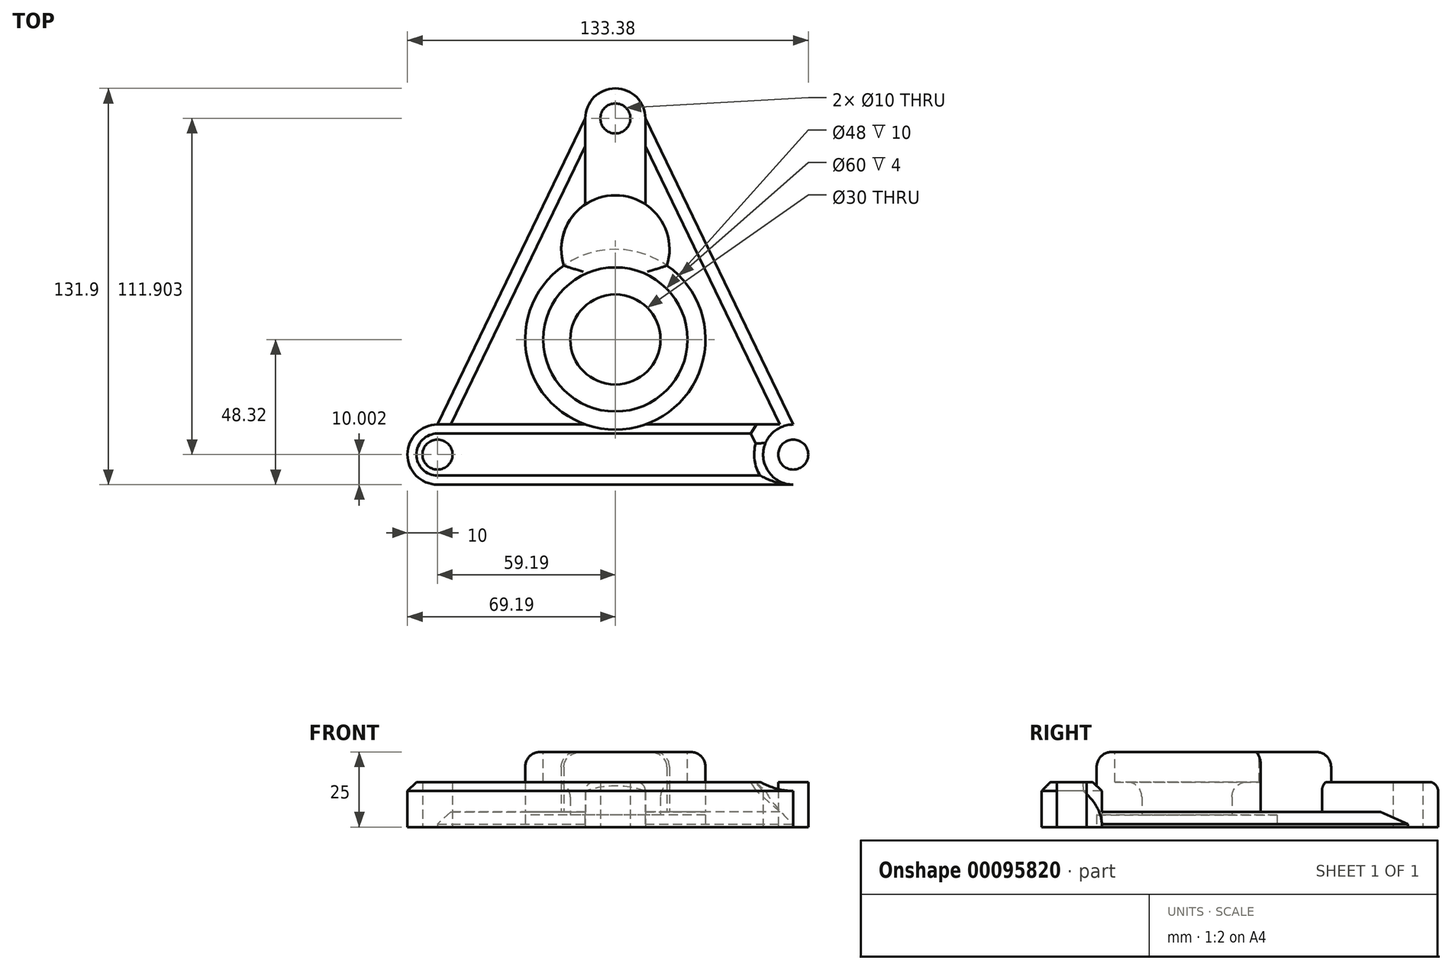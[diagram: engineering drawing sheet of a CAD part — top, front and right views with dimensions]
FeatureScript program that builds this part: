
annotation { "Feature Type Name" : "Feature", "Feature Type Description" : "" }
export const myFeature = defineFeature(function(context is Context, id is Id, definition is map)
    precondition{}
    {
        {
            var Q0;
            Q0=qCreatedBy(makeId("Top.planeOp"),FACE);
            var sketch = newSketch(context, id + "F0", { "sketchPlane" : qUnion([Q0])});
            skLineSegment(sketch, "E0", {"start": v(0, 62.87) * mm, "end": v(0, -63.53) * mm, "construction": true});
            skLineSegment(sketch, "E1", {"start": v(-118.77, -38.32) * mm, "end": v(118.1, -38.32) * mm, "construction": true});
            skCircle(sketch, "E2", {"center": v(0, 0) * mm, "radius": 15 * mm});
            skCircle(sketch, "E3", {"center": v(0, 0) * mm, "radius": 18 * mm});
            skCircle(sketch, "E4", {"center": v(0, 0) * mm, "radius": 24 * mm});
            skCircle(sketch, "E5", {"center": v(0, 0) * mm, "radius": 30 * mm});
            skCircle(sketch, "E6", {"center": v(0, 30) * mm, "radius": 8 * mm});
            skCircle(sketch, "E7", {"center": v(0, 30) * mm, "radius": 11 * mm});
            skArc(sketch, "E8", {"start": v(17.17, 24.6) * mm, "mid": v(0, 48) * mm, "end": v(-17.17, 24.6) * mm});
            skCircle(sketch, "E9", {"center": v(0, 73.58) * mm, "radius": 5 * mm});
            skCircle(sketch, "E10", {"center": v(0, 73.58) * mm, "radius": 10 * mm});
            skCircle(sketch, "E11", {"center": v(-59.2, -38.32) * mm, "radius": 10 * mm});
            skCircle(sketch, "E12", {"center": v(-59.2, -38.32) * mm, "radius": 5 * mm});
            skCircle(sketch, "E13.MirrorC", {"center": v(59.2, -38.32) * mm, "radius": 5 * mm});
            skCircle(sketch, "E14.MirrorC", {"center": v(59.2, -38.32) * mm, "radius": 10 * mm});
            skLineSegment(sketch, "E15", {"start": v(-10, 73.58) * mm, "end": v(-10, 44.97) * mm});
            skLineSegment(sketch, "E16", {"start": v(-59.2, -28.32) * mm, "end": v(-9.9, -28.32) * mm});
            skLineSegment(sketch, "E17", {"start": v(-10, 73.58) * mm, "end": v(-59.2, -28.32) * mm});
            skLineSegment(sketch, "E18", {"start": v(-59.2, -48.32) * mm, "end": v(0, -48.32) * mm});
            skLineSegment(sketch, "E19.MirrorCS", {"start": v(59.2, -48.32) * mm, "end": v(0, -48.32) * mm});
            skLineSegment(sketch, "E20.MirrorCS", {"start": v(59.2, -28.32) * mm, "end": v(9.9, -28.32) * mm});
            skLineSegment(sketch, "E21.MirrorCS", {"start": v(10, 73.58) * mm, "end": v(59.2, -28.32) * mm});
            skLineSegment(sketch, "E22.MirrorCS", {"start": v(10, 73.58) * mm, "end": v(10, 44.97) * mm});
            skSolve(sketch);
        }
        {
            var Q0;
            {var subQ0=sQuery(id+"F0.wireOp",EDGE,"E8");var subQ1=sQuery(id+"F0.wireOp",EDGE,"E5");var subQ5=makeQuery(id+"F0.imprint","INTERSECT",VERTEX,{"disambiguationData":[OD(0.0)],"derivedFrom":[subQ1,subQ0]});Q0=makeQuery(id+"F0.imprint","IMPRINT",FACE,{"disambiguationData":[TD([[makeQuery(id+"F0.imprint","IMPRINT",EDGE,{"disambiguationData":[TD([[subQ5,-1.0]])],"derivedFrom":subQ1}),-1.0]])]});}
            var Q1;
            {var subQ0=sQuery(id+"F0.wireOp",EDGE,"E6");var subQ1=sQuery(id+"F0.wireOp",EDGE,"E5");var subQ2=makeQuery(id+"F0.imprint","INTERSECT",VERTEX,{"disambiguationData":[OD(0.0)],"derivedFrom":[subQ1,subQ0]});Q1=makeQuery(id+"F0.imprint","IMPRINT",FACE,{"disambiguationData":[TD([[makeQuery(id+"F0.imprint","IMPRINT",EDGE,{"disambiguationData":[TD([[subQ2,-1.0]])],"derivedFrom":subQ1}),-1.0]])]});}
            var Q2;
            {var subQ0=sQuery(id+"F0.wireOp",EDGE,"E7");var subQ1=sQuery(id+"F0.wireOp",EDGE,"E5");var subQ2=makeQuery(id+"F0.imprint","INTERSECT",VERTEX,{"disambiguationData":[OD(0.0)],"derivedFrom":[subQ1,subQ0]});Q2=makeQuery(id+"F0.imprint","IMPRINT",FACE,{"disambiguationData":[TD([[makeQuery(id+"F0.imprint","IMPRINT",EDGE,{"disambiguationData":[TD([[subQ2,-1.0]])],"derivedFrom":subQ1}),-1.0]])]});}
            var Q3;
            {var subQ4=sQuery(id+"F0.wireOp",EDGE,"E7");var subQ9=sQuery(id+"F0.wireOp",EDGE,"E4");var subQ10=makeQuery(id+"F0.imprint","INTERSECT",VERTEX,{"disambiguationData":[OD(0.0)],"derivedFrom":[subQ9,subQ4]});Q3=makeQuery(id+"F0.imprint","IMPRINT",FACE,{"disambiguationData":[TD([[makeQuery(id+"F0.imprint","IMPRINT",EDGE,{"disambiguationData":[TD([[subQ10,1.0]])],"derivedFrom":subQ9}),-1.0]])]});}
            var Q4;
            Q4=makeQuery(id+"F0.imprint","IMPRINT",FACE,{"disambiguationData":[TD([[makeQuery(id+"F0.imprint","IMPRINT",EDGE,{"derivedFrom":sQuery(id+"F0.wireOp",EDGE,"E3")}),-1.0]])]});
            var Q5;
            Q5=makeQuery(id+"F0.imprint","IMPRINT",FACE,{"disambiguationData":[TD([[makeQuery(id+"F0.imprint","IMPRINT",EDGE,{"derivedFrom":sQuery(id+"F0.wireOp",EDGE,"E2")}),-1.0]])]});
            var Q6;
            Q6=makeQuery(id+"F0.imprint","IMPRINT",FACE,{"disambiguationData":[TD([[makeQuery(id+"F0.imprint","IMPRINT",EDGE,{"derivedFrom":sQuery(id+"F0.wireOp",EDGE,"E2")}),1.0]])]});
            var Q7;
            {var subQ0=sQuery(id+"F0.wireOp",EDGE,"E6");var subQ1=sQuery(id+"F0.wireOp",EDGE,"E4");var subQ2=makeQuery(id+"F0.imprint","INTERSECT",VERTEX,{"disambiguationData":[OD(0.0)],"derivedFrom":[subQ1,subQ0]});Q7=makeQuery(id+"F0.imprint","IMPRINT",FACE,{"disambiguationData":[TD([[makeQuery(id+"F0.imprint","IMPRINT",EDGE,{"disambiguationData":[TD([[subQ2,1.0]])],"derivedFrom":subQ1}),1.0]])]});}
            var Q8;
            {var subQ0=sQuery(id+"F0.wireOp",EDGE,"E6");var subQ1=sQuery(id+"F0.wireOp",EDGE,"E4");var subQ2=makeQuery(id+"F0.imprint","INTERSECT",VERTEX,{"disambiguationData":[OD(0.0)],"derivedFrom":[subQ1,subQ0]});Q8=makeQuery(id+"F0.imprint","IMPRINT",FACE,{"disambiguationData":[TD([[makeQuery(id+"F0.imprint","IMPRINT",EDGE,{"disambiguationData":[TD([[subQ2,1.0]])],"derivedFrom":subQ1}),-1.0]])]});}
            var Q9;
            {var subQ0=sQuery(id+"F0.wireOp",EDGE,"E6");var subQ1=sQuery(id+"F0.wireOp",EDGE,"E4");var subQ2=makeQuery(id+"F0.imprint","INTERSECT",VERTEX,{"disambiguationData":[OD(1.0)],"derivedFrom":[subQ1,subQ0]});Q9=makeQuery(id+"F0.imprint","IMPRINT",FACE,{"disambiguationData":[TD([[makeQuery(id+"F0.imprint","IMPRINT",EDGE,{"disambiguationData":[TD([[subQ2,-1.0]])],"derivedFrom":subQ1}),-1.0]])]});}
            var Q10;
            {var subQ0=sQuery(id+"F0.wireOp",EDGE,"E6");var subQ1=sQuery(id+"F0.wireOp",EDGE,"E4");var subQ2=makeQuery(id+"F0.imprint","INTERSECT",VERTEX,{"disambiguationData":[OD(0.0)],"derivedFrom":[subQ1,subQ0]});Q10=makeQuery(id+"F0.imprint","IMPRINT",FACE,{"disambiguationData":[TD([[makeQuery(id+"F0.imprint","IMPRINT",EDGE,{"disambiguationData":[TD([[subQ2,-1.0]])],"derivedFrom":subQ1}),-1.0]])]});}
            var Q11;
            {var subQ0=sQuery(id+"F0.wireOp",EDGE,"E6");var subQ1=sQuery(id+"F0.wireOp",EDGE,"E4");var subQ2=makeQuery(id+"F0.imprint","INTERSECT",VERTEX,{"disambiguationData":[OD(0.0)],"derivedFrom":[subQ1,subQ0]});Q11=makeQuery(id+"F0.imprint","IMPRINT",FACE,{"disambiguationData":[TD([[makeQuery(id+"F0.imprint","IMPRINT",EDGE,{"disambiguationData":[TD([[subQ2,-1.0]])],"derivedFrom":subQ1}),1.0]])]});}
            extrude(context, id + "F1", {"entities" : qUnion([Q0, Q1, Q2, Q3, Q4, Q5, Q6, Q7, Q8, Q9, Q10, Q11]), "depth" : 25 * mm});
        }
        {
            var Q0;
            {var subQ0=sQuery(id+"F0.wireOp",EDGE,"E16");Q0=makeQuery(id+"F0.imprint","IMPRINT",FACE,{"disambiguationData":[TD([[makeQuery(id+"F0.imprint","IMPRINT",EDGE,{"derivedFrom":subQ0}),-1.0]])]});}
            var Q1;
            Q1=makeQuery(id+"F0.imprint","IMPRINT",FACE,{"disambiguationData":[TD([[makeQuery(id+"F0.imprint","IMPRINT",EDGE,{"derivedFrom":sQuery(id+"F0.wireOp",EDGE,"E12")}),-1.0]])]});
            var Q2;
            Q2=makeQuery(id+"F0.imprint","IMPRINT",FACE,{"disambiguationData":[TD([[makeQuery(id+"F0.imprint","IMPRINT",EDGE,{"derivedFrom":sQuery(id+"F0.wireOp",EDGE,"E13.MirrorC")}),1.0]])]});
            var Q3;
            {var subQ0=sQuery(id+"F0.wireOp",EDGE,"E15");Q3=makeQuery(id+"F0.imprint","IMPRINT",FACE,{"disambiguationData":[TD([[makeQuery(id+"F0.imprint","IMPRINT",EDGE,{"derivedFrom":subQ0}),1.0]])]});}
            var Q4;
            Q4=makeQuery(id+"F0.imprint","IMPRINT",FACE,{"disambiguationData":[TD([[makeQuery(id+"F0.imprint","IMPRINT",EDGE,{"derivedFrom":sQuery(id+"F0.wireOp",EDGE,"E9")}),-1.0]])]});
            extrude(context, id + "F2", {"entities" : qUnion([Q0, Q1, Q2, Q3, Q4]), "operationType" : NewBodyOperationType.ADD, "depth" : 15 * mm});
        }
        {
            var Q0;
            {var subQ1=sQuery(id+"F0.wireOp",EDGE,"E15");Q0=makeQuery(id+"F0.imprint","IMPRINT",FACE,{"disambiguationData":[TD([[makeQuery(id+"F0.imprint","IMPRINT",EDGE,{"derivedFrom":subQ1}),-1.0]])]});}
            var Q1;
            {var subQ4=sQuery(id+"F0.wireOp",EDGE,"E20.MirrorCS");Q1=makeQuery(id+"F0.imprint","IMPRINT",FACE,{"disambiguationData":[TD([[makeQuery(id+"F0.imprint","IMPRINT",EDGE,{"derivedFrom":subQ4}),-1.0]])]});}
            extrude(context, id + "F3", {"entities" : qUnion([Q0, Q1]), "operationType" : NewBodyOperationType.ADD, "depth" : 5 * mm});
        }
        {
            var Q0;
            Q0=makeQuery(id+"F1.opExtrude","CAP_FACE",FACE,{"disambiguationData":[OSD([sQuery(id+"F0.wireOp",EDGE,"E5"),sQuery(id+"F0.wireOp",EDGE,"E8")])],"isStart":false});
            var sketch = newSketch(context, id + "F4", { "sketchPlane" : qUnion([Q0])});
            skCircle(sketch, "E23.0", {"center": v(0, 0) * mm, "radius": 24 * mm});
            skSolve(sketch);
        }
        {
            var Q0;
            Q0 = qSketchRegion(id + "F4", true);
            extrude(context, id + "F5", {"entities" : qUnion([Q0]), "operationType" : NewBodyOperationType.REMOVE, "oppositeDirection" : true, "depth" : 10 * mm});
        }
        {
            var Q0;
            Q0=makeQuery(id+"F0.imprint","IMPRINT",FACE,{"disambiguationData":[TD([[makeQuery(id+"F0.imprint","IMPRINT",EDGE,{"derivedFrom":sQuery(id+"F0.wireOp",EDGE,"E3")}),-1.0]])]});
            var sketch = newSketch(context, id + "F6", { "sketchPlane" : qUnion([Q0])});
            skArc(sketch, "E24.0.0", {"start": v(8.12, 22.58) * mm, "mid": v(0, -24) * mm, "end": v(-8.12, 22.58) * mm});
            skArc(sketch, "E24.0.1", {"start": v(-8.12, 22.58) * mm, "mid": v(-9.85, 25.1) * mm, "end": v(-10.81, 27.98) * mm});
            skArc(sketch, "E24.0.2", {"start": v(-10.81, 27.98) * mm, "mid": v(-14.1, 26.48) * mm, "end": v(-17.17, 24.6) * mm});
            skArc(sketch, "E24.0.3", {"start": v(-17.17, 24.6) * mm, "mid": v(-29.72, -4.08) * mm, "end": v(-9.9, -28.32) * mm});
            skArc(sketch, "E24.0.4", {"start": v(-9.9, -28.32) * mm, "mid": v(0, -30) * mm, "end": v(9.9, -28.32) * mm});
            skArc(sketch, "E24.0.5", {"start": v(9.9, -28.32) * mm, "mid": v(29.72, -4.08) * mm, "end": v(17.17, 24.6) * mm});
            skArc(sketch, "E24.0.6", {"start": v(17.17, 24.6) * mm, "mid": v(14.1, 26.48) * mm, "end": v(10.81, 27.98) * mm});
            skArc(sketch, "E24.0.7", {"start": v(10.81, 27.98) * mm, "mid": v(9.85, 25.1) * mm, "end": v(8.12, 22.58) * mm});
            skSolve(sketch);
        }
        {
            var Q0;
            Q0 = qSketchRegion(id + "F6", true);
            var Q1;
            {var subQ0=sQuery(id+"F0.wireOp",EDGE,"E6");var subQ1=sQuery(id+"F0.wireOp",EDGE,"E4");var subQ2=makeQuery(id+"F0.imprint","INTERSECT",VERTEX,{"disambiguationData":[OD(0.0)],"derivedFrom":[subQ1,subQ0]});Q1=makeQuery(id+"F0.imprint","IMPRINT",FACE,{"disambiguationData":[TD([[makeQuery(id+"F0.imprint","IMPRINT",EDGE,{"disambiguationData":[TD([[subQ2,-1.0]])],"derivedFrom":subQ1}),-1.0]])]});}
            var Q2;
            {var subQ0=sQuery(id+"F0.wireOp",EDGE,"E6");var subQ1=sQuery(id+"F0.wireOp",EDGE,"E4");var subQ2=makeQuery(id+"F0.imprint","INTERSECT",VERTEX,{"disambiguationData":[OD(1.0)],"derivedFrom":[subQ1,subQ0]});Q2=makeQuery(id+"F0.imprint","IMPRINT",FACE,{"disambiguationData":[TD([[makeQuery(id+"F0.imprint","IMPRINT",EDGE,{"disambiguationData":[TD([[subQ2,-1.0]])],"derivedFrom":subQ1}),-1.0]])]});}
            var Q3;
            Q3=makeQuery(id+"F0.imprint","IMPRINT",FACE,{"disambiguationData":[TD([[makeQuery(id+"F0.imprint","IMPRINT",EDGE,{"derivedFrom":sQuery(id+"F0.wireOp",EDGE,"E2")}),-1.0]])]});
            var Q4;
            Q4=makeQuery(id+"F6.imprint","IMPRINT",FACE,{"disambiguationData":[TD([[makeQuery(id+"F6.imprint","IMPRINT",EDGE,{"derivedFrom":makeQuery(id+"F0.imprint","IMPRINT",EDGE,{"derivedFrom":sQuery(id+"F0.wireOp",EDGE,"E3")})}),1.0]])]});
            var Q5;
            Q5=makeQuery(id+"F0.imprint","IMPRINT",FACE,{"disambiguationData":[TD([[makeQuery(id+"F0.imprint","IMPRINT",EDGE,{"derivedFrom":sQuery(id+"F0.wireOp",EDGE,"E3")}),-1.0]])]});
            var Q6;
            {var subQ0=sQuery(id+"F0.wireOp",EDGE,"E6");var subQ1=sQuery(id+"F0.wireOp",EDGE,"E4");var subQ2=makeQuery(id+"F0.imprint","INTERSECT",VERTEX,{"disambiguationData":[OD(0.0)],"derivedFrom":[subQ1,subQ0]});Q6=makeQuery(id+"F0.imprint","IMPRINT",FACE,{"disambiguationData":[TD([[makeQuery(id+"F0.imprint","IMPRINT",EDGE,{"disambiguationData":[TD([[subQ2,1.0]])],"derivedFrom":subQ1}),-1.0]])]});}
            var Q7;
            {var subQ0=sQuery(id+"F0.wireOp",EDGE,"E6");var subQ1=sQuery(id+"F0.wireOp",EDGE,"E4");var subQ2=makeQuery(id+"F0.imprint","INTERSECT",VERTEX,{"disambiguationData":[OD(0.0)],"derivedFrom":[subQ1,subQ0]});Q7=makeQuery(id+"F0.imprint","IMPRINT",FACE,{"disambiguationData":[TD([[makeQuery(id+"F0.imprint","IMPRINT",EDGE,{"disambiguationData":[TD([[subQ2,1.0]])],"derivedFrom":subQ1}),1.0]])]});}
            var Q8;
            {var subQ0=sQuery(id+"F0.wireOp",EDGE,"E6");var subQ1=sQuery(id+"F0.wireOp",EDGE,"E4");var subQ2=makeQuery(id+"F0.imprint","INTERSECT",VERTEX,{"disambiguationData":[OD(0.0)],"derivedFrom":[subQ1,subQ0]});Q8=makeQuery(id+"F0.imprint","IMPRINT",FACE,{"disambiguationData":[TD([[makeQuery(id+"F0.imprint","IMPRINT",EDGE,{"disambiguationData":[TD([[subQ2,-1.0]])],"derivedFrom":subQ1}),1.0]])]});}
            extrude(context, id + "F7", {"entities" : qUnion([Q0, Q1, Q2, Q3, Q4, Q5, Q6, Q7, Q8]), "operationType" : NewBodyOperationType.REMOVE, "depth" : 4 * mm});
        }
        {
            var Q0;
            Q0=makeQuery(id+"F0.imprint","IMPRINT",FACE,{"disambiguationData":[TD([[makeQuery(id+"F0.imprint","IMPRINT",EDGE,{"derivedFrom":sQuery(id+"F0.wireOp",EDGE,"E2")}),1.0]])]});
            var Q1;
            Q1=sQuery(id+"F0.wireOp",EDGE,"E2");
            extrude(context, id + "F8", {"entities" : qUnion([Q0]), "operationType" : NewBodyOperationType.REMOVE, "surfaceEntities" : qUnion([Q1]), "depth" : 25 * mm});
        }
        {
            var Q0;
            Q0=makeQuery(id+"F5.boolean.opBoolean","COPY",EDGE,{"derivedFrom":makeQuery(id+"F5.opExtrude","CAP_EDGE",EDGE,{"disambiguationData":[OSD([sQuery(id+"F4.wireOp",EDGE,"E23.0")])],"isStart":true})});
            var Q1;
            Q1=makeQuery(id+"F1.opExtrude","CAP_EDGE",EDGE,{"disambiguationData":[OSD([sQuery(id+"F0.wireOp",EDGE,"E5")])],"isStart":false});
            var Q2;
            Q2=makeQuery(id+"F1.opExtrude","CAP_EDGE",EDGE,{"disambiguationData":[OSD([sQuery(id+"F0.wireOp",EDGE,"E8")])],"isStart":false});
            fillet(context, id + "F9", {"entities" : qUnion([Q0, Q1, Q2]), "radius" : 5 * mm, "tangentPropagation" : true, "allowEdgeOverflow" : false});
        }
        {
            var Q0;
            Q0=makeQuery(id+"F8.boolean.opBoolean","INTERSECT",EDGE,{"derivedFrom":[makeQuery(id+"F5.boolean.opBoolean","COPY",FACE,{"derivedFrom":makeQuery(id+"F5.opExtrude","CAP_FACE",FACE,{"disambiguationData":[OSD([sQuery(id+"F4.wireOp",EDGE,"E23.0")])],"isStart":false})}),makeQuery(id+"F8.opExtrude","SWEPT_FACE",FACE,{"disambiguationData":[OSD([sQuery(id+"F0.wireOp",EDGE,"E2")])]})]});
            fillet(context, id + "F10", {"entities" : qUnion([Q0]), "radius" : 5 * mm, "tangentPropagation" : true, "allowEdgeOverflow" : false});
        }
        {
            var Q0;
            Q0=makeQuery(id+"F3.opExtrude","CAP_EDGE",EDGE,{"disambiguationData":[OSD([sQuery(id+"F0.wireOp",EDGE,"E21.MirrorCS")])],"isStart":false});
            var Q1;
            Q1=makeQuery(id+"F3.opExtrude","CAP_EDGE",EDGE,{"disambiguationData":[OSD([sQuery(id+"F0.wireOp",EDGE,"E17")])],"isStart":false});
            chamfer(context, id + "F11", {"entities" : qUnion([Q0, Q1]), "width" : 4 * mm, "tangentPropagation" : true});
        }
        {
            var Q0;
            Q0=makeQuery(id+"F2.opExtrude","CAP_EDGE",EDGE,{"disambiguationData":[OSD([sQuery(id+"F0.wireOp",EDGE,"E11")])],"isStart":false});
            var Q1;
            Q1=makeQuery(id+"F2.opExtrude","CAP_EDGE",EDGE,{"disambiguationData":[OSD([sQuery(id+"F0.wireOp",EDGE,"E18"),sQuery(id+"F0.wireOp",EDGE,"E19.MirrorCS")])],"isStart":false});
            var Q2;
            Q2=makeQuery(id+"F2.opExtrude","CAP_EDGE",EDGE,{"disambiguationData":[OSD([sQuery(id+"F0.wireOp",EDGE,"E14.MirrorC")])],"isStart":false});
            chamfer(context, id + "F12", {"entities" : qUnion([Q0, Q1, Q2]), "width" : 3 * mm, "tangentPropagation" : true});
        }
        {
            var Q0;
            Q0=makeQuery(id+"F2.opExtrude","CAP_EDGE",EDGE,{"disambiguationData":[OSD([sQuery(id+"F0.wireOp",EDGE,"E22.MirrorCS")])],"isStart":false});
            var Q1;
            Q1=makeQuery(id+"F2.opExtrude","CAP_EDGE",EDGE,{"disambiguationData":[OSD([sQuery(id+"F0.wireOp",EDGE,"E15")])],"isStart":false});
            var Q2;
            Q2=makeQuery(id+"F2.opExtrude","CAP_EDGE",EDGE,{"disambiguationData":[OSD([sQuery(id+"F0.wireOp",EDGE,"E10")])],"isStart":false});
            fillet(context, id + "F13", {"entities" : qUnion([Q0, Q1, Q2]), "radius" : 3 * mm, "tangentPropagation" : true, "allowEdgeOverflow" : false});
        }
    });
